# Revit family: WL212-swnew
name_source: partatom
category: Communication Devices
revit_build: Autodesk Revit Architecture 2012 (Build: 20110309_2315(x64)
units: mm (PartAtom-declared; Revit-internal decimal feet)

## types (1)
- WL212-swnew
    Default Elevation = 0.000"
    Depth = 29.000"
    Description = Dual 12" Bandpass Subwoofer
    Enclosure Finish = Black Finish
    Enclosure Width = 20.000"
    Front Rigging Collision Zone Front Offset = 0.332"
    Front Rigging Collision Zone Rear Offset = 2.551"
    Height = 15.000"
    Impedance = 4
    Manufacturer = QSC Audio Products, LLC
    Manufacturer URL = www.qscaudio.com
    Model = WL212-sw
    Port Depth = -28.400"
    Power Handling = 1100
    Product Documentation Link = http://media.qscaudio.com
    Product Page URL = http://www.qscaudio.com
    Rear Rigging Collision Zone Front Offset = 11.926"
    Rear Rigging Collision Zone Rear Offset = 15.801"
    Regulatory Compliance = RoHS
    Rigging Collision Zone Finish = Black Finish
    Rigging Collision Zone Width = 0.850"
    SPL Max = 135
    Sensitivity = 99
    URL = http://www.qscaudio.com
    Weight Dimensional (kg) = 56.7
    Weight Dimensional (lb) = 125
    Weight Product (kg) = 49.4
    Weight Product (lb) = 109
    Width = 21.700"

## geometry (parser evidence)
native form markers: Blend x1, Sweep x1
no freeform markers — native parametric forms only
